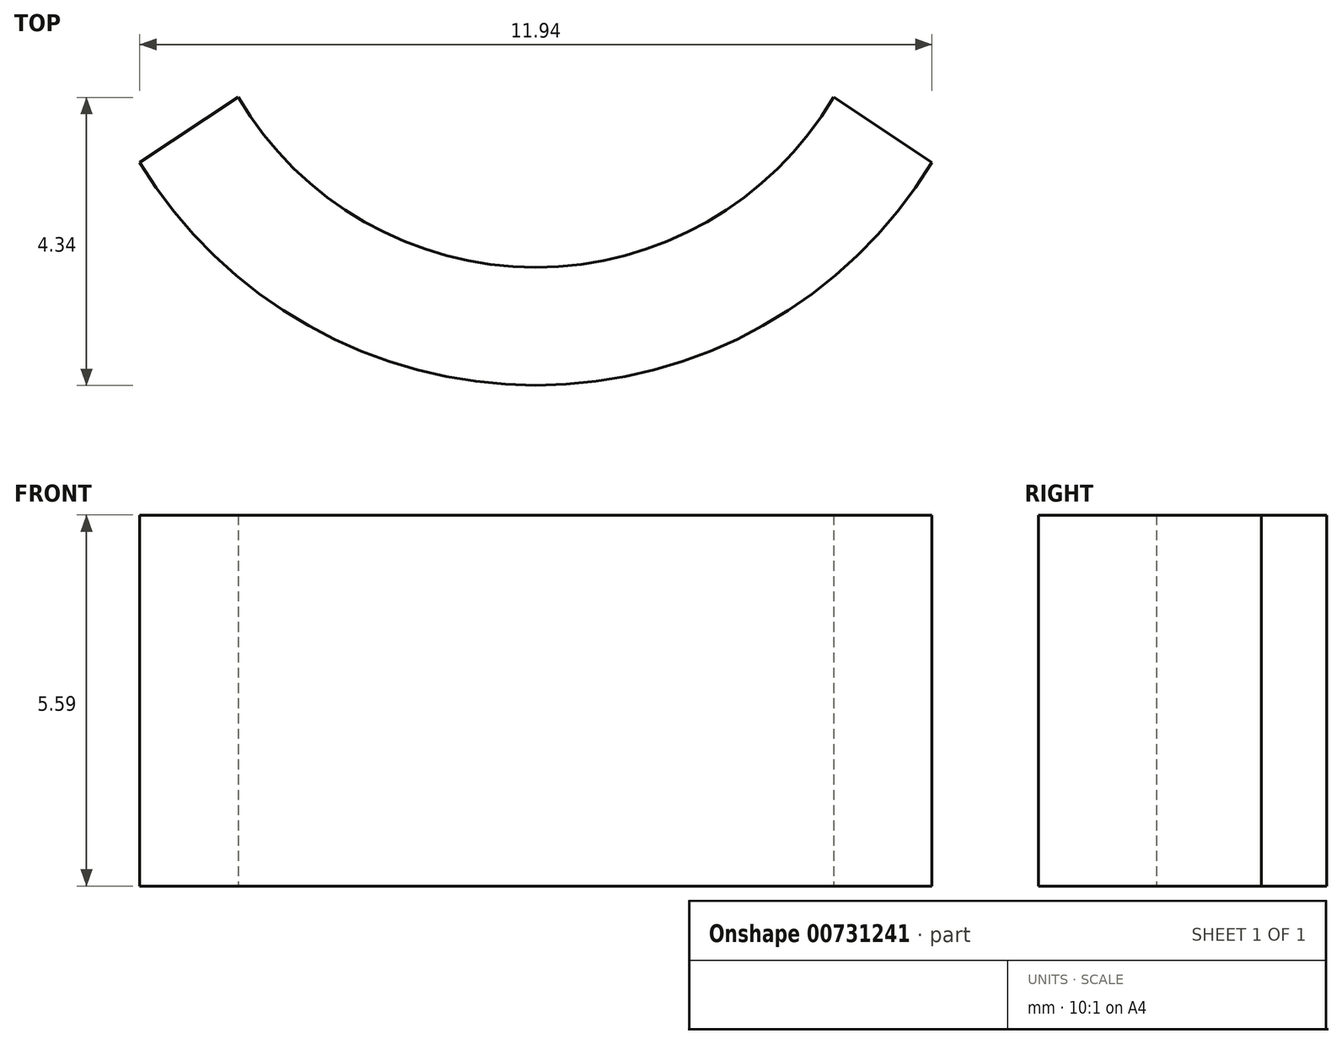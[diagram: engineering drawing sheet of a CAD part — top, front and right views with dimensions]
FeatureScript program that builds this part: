
annotation { "Feature Type Name" : "Feature", "Feature Type Description" : "" }
export const myFeature = defineFeature(function(context is Context, id is Id, definition is map)
    precondition{}
    {
        {
            var Q0;
            Q0=qCreatedBy(makeId("Top.planeOp"),FACE);
            var sketch = newSketch(context, id + "F0", { "sketchPlane" : qUnion([Q0])});
            skArc(sketch, "E0", {"start": v(0, 0) * mm, "mid": v(5.97, -3.36) * mm, "end": v(11.94, 0) * mm});
            skArc(sketch, "E1.0", {"start": v(1.48, 0.98) * mm, "mid": v(5.97, -1.58) * mm, "end": v(10.46, 0.98) * mm});
            skLineSegment(sketch, "E2", {"start": v(1.48, 0.98) * mm, "end": v(0, 0) * mm});
            skLineSegment(sketch, "E3", {"start": v(10.46, 0.98) * mm, "end": v(11.94, 0) * mm});
            skSolve(sketch);
        }
        {
            var Q0;
            Q0 = qSketchRegion(id + "F0", true);
            extrude(context, id + "F1", {"entities" : qUnion([Q0]), "depth" : 5.6 * mm, "offsetDistance" : 25.4 * mm});
        }
    });
